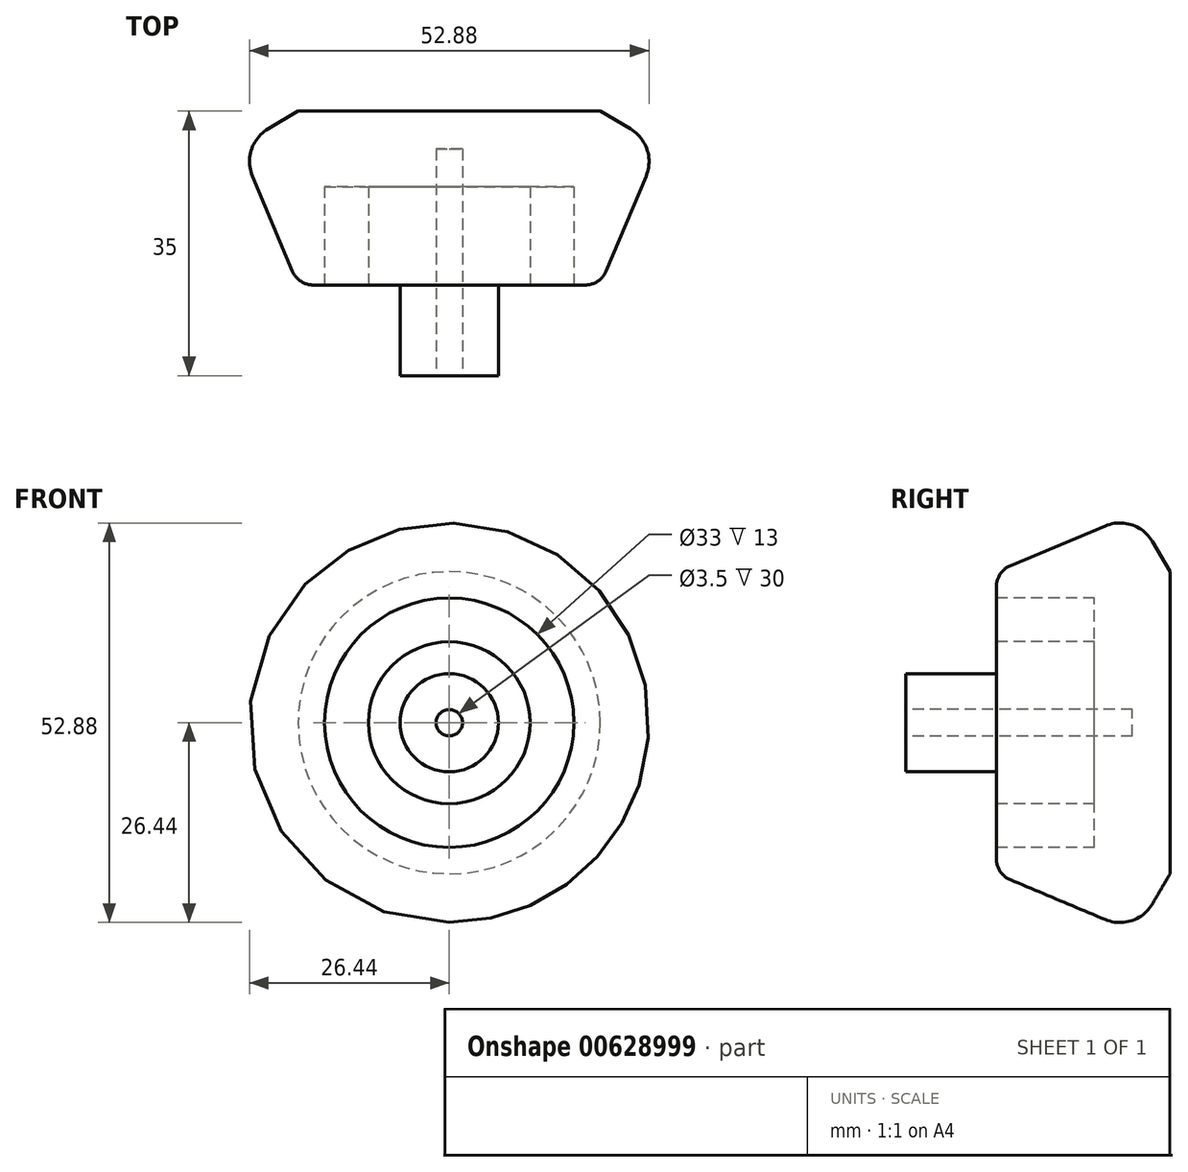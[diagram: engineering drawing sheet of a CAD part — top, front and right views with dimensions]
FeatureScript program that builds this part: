
annotation { "Feature Type Name" : "Feature", "Feature Type Description" : "" }
export const myFeature = defineFeature(function(context is Context, id is Id, definition is map)
    precondition{}
    {
        {
            var Q0;
            Q0=qCreatedBy(makeId("Front.planeOp"),FACE);
            var sketch = newSketch(context, id + "F0", { "sketchPlane" : qUnion([Q0])});
            skCircle(sketch, "E0", {"center": v(0, 0) * mm, "radius": 1.75 * mm});
            skCircle(sketch, "E1", {"center": v(0, 0) * mm, "radius": 6.5 * mm});
            skSolve(sketch);
        }
        {
            var Q0;
            Q0=qCreatedBy(makeId("Right.planeOp"),FACE);
            var sketch = newSketch(context, id + "F1", { "sketchPlane" : qUnion([Q0])});
            skLineSegment(sketch, "E2", {"start": v(0, 9.44) * mm, "end": v(0, -12.72) * mm, "construction": true});
            skLineSegment(sketch, "E3", {"start": v(12, 9.44) * mm, "end": v(12, -12.24) * mm, "construction": true});
            skLineSegment(sketch, "E4", {"start": v(35, 9.44) * mm, "end": v(35, -12.24) * mm, "construction": true});
            skLineSegment(sketch, "E5", {"start": v(12, 0) * mm, "end": v(12, 20) * mm});
            skLineSegment(sketch, "E6", {"start": v(35, 0) * mm, "end": v(12, 0) * mm});
            skLineSegment(sketch, "E7", {"start": v(5.3, 0) * mm, "end": v(66.6, 0) * mm, "construction": true});
            skLineSegment(sketch, "E8", {"start": v(35, 20) * mm, "end": v(35, 0) * mm});
            skLineSegment(sketch, "E9", {"start": v(12, 20) * mm, "end": v(30.44, 27.74) * mm});
            skLineSegment(sketch, "E10", {"start": v(30.44, 27.74) * mm, "end": v(35, 20) * mm});
            skSolve(sketch);
        }
        {
            var Q0;
            Q0=makeQuery(id+"F1.imprint","IMPRINT",FACE,{"disambiguationData":[TD([[makeQuery(id+"F1.imprint","IMPRINT",EDGE,{"derivedFrom":sQuery(id+"F1.wireOp",EDGE,"E5")}),-1.0]])]});
            var Q1;
            Q1=sQuery(id+"F1.wireOp",EDGE,"E7");
            revolve(context, id + "F2", {"entities" : qUnion([Q0]), "axis" : qUnion([Q1]), "revolveType" : RevolveType.FULL});
        }
        {
            var Q0;
            Q0=makeQuery(id+"F0.imprint","IMPRINT",FACE,{"disambiguationData":[TD([[makeQuery(id+"F0.imprint","IMPRINT",EDGE,{"derivedFrom":sQuery(id+"F0.wireOp",EDGE,"E0")}),-1.0]])]});
            extrude(context, id + "F3", {"entities" : qUnion([Q0]), "operationType" : NewBodyOperationType.ADD, "oppositeDirection" : true, "depth" : 20 * mm, "offsetDistance" : 25 * mm});
        }
        {
            var Q0;
            Q0=makeQuery(id+"F0.imprint","IMPRINT",FACE,{"disambiguationData":[TD([[makeQuery(id+"F0.imprint","IMPRINT",EDGE,{"derivedFrom":sQuery(id+"F0.wireOp",EDGE,"E0")}),1.0]])]});
            extrude(context, id + "F4", {"entities" : qUnion([Q0]), "operationType" : NewBodyOperationType.REMOVE, "oppositeDirection" : true, "depth" : 30 * mm, "offsetDistance" : 25 * mm});
        }
        {
            var Q0;
            Q0=makeQuery(id+"F2.opRevolve","SWEPT_EDGE",EDGE,{"disambiguationData":[OSD([sQuery(id+"F1.wireOp",EDGE,"E5"),sQuery(id+"F1.wireOp",EDGE,"ZsN8Qygy-ZeGg-ojcV-Q1XJ-PC7i1hJ47Dko")])]});
            fillet(context, id + "F5", {"entities" : qUnion([Q0]), "radius" : 3 * mm, "tangentPropagation" : true, "allowEdgeOverflow" : false});
        }
        {
            var Q0;
            Q0=makeQuery(id+"F2.opRevolve","SWEPT_EDGE",EDGE,{"disambiguationData":[OSD([sQuery(id+"F1.wireOp",EDGE,"E9"),sQuery(id+"F1.wireOp",EDGE,"E10")])]});
            fillet(context, id + "F6", {"entities" : qUnion([Q0]), "radius" : 5 * mm, "tangentPropagation" : true, "allowEdgeOverflow" : false});
        }
        {
            var Q0;
            Q0=qCreatedBy(makeId("Front.planeOp"),FACE);
            var sketch = newSketch(context, id + "F7", { "sketchPlane" : qUnion([Q0])});
            skCircle(sketch, "E11", {"center": v(0, 0) * mm, "radius": 10.7 * mm});
            skCircle(sketch, "E12", {"center": v(0, 0) * mm, "radius": 16.5 * mm});
            skSolve(sketch);
        }
        {
            var Q0;
            Q0 = qSketchRegion(id + "F7", true);
            var Q1;
            Q1=makeQuery(id+"F7.imprint","IMPRINT",FACE,{"disambiguationData":[TD([[makeQuery(id+"F7.imprint","IMPRINT",EDGE,{"derivedFrom":sQuery(id+"F7.wireOp",EDGE,"E11")}),-1.0]])]});
            extrude(context, id + "F8", {"entities" : qUnion([Q0, Q1]), "operationType" : NewBodyOperationType.REMOVE, "oppositeDirection" : true, "depth" : 25 * mm, "offsetDistance" : 25 * mm});
        }
    });
